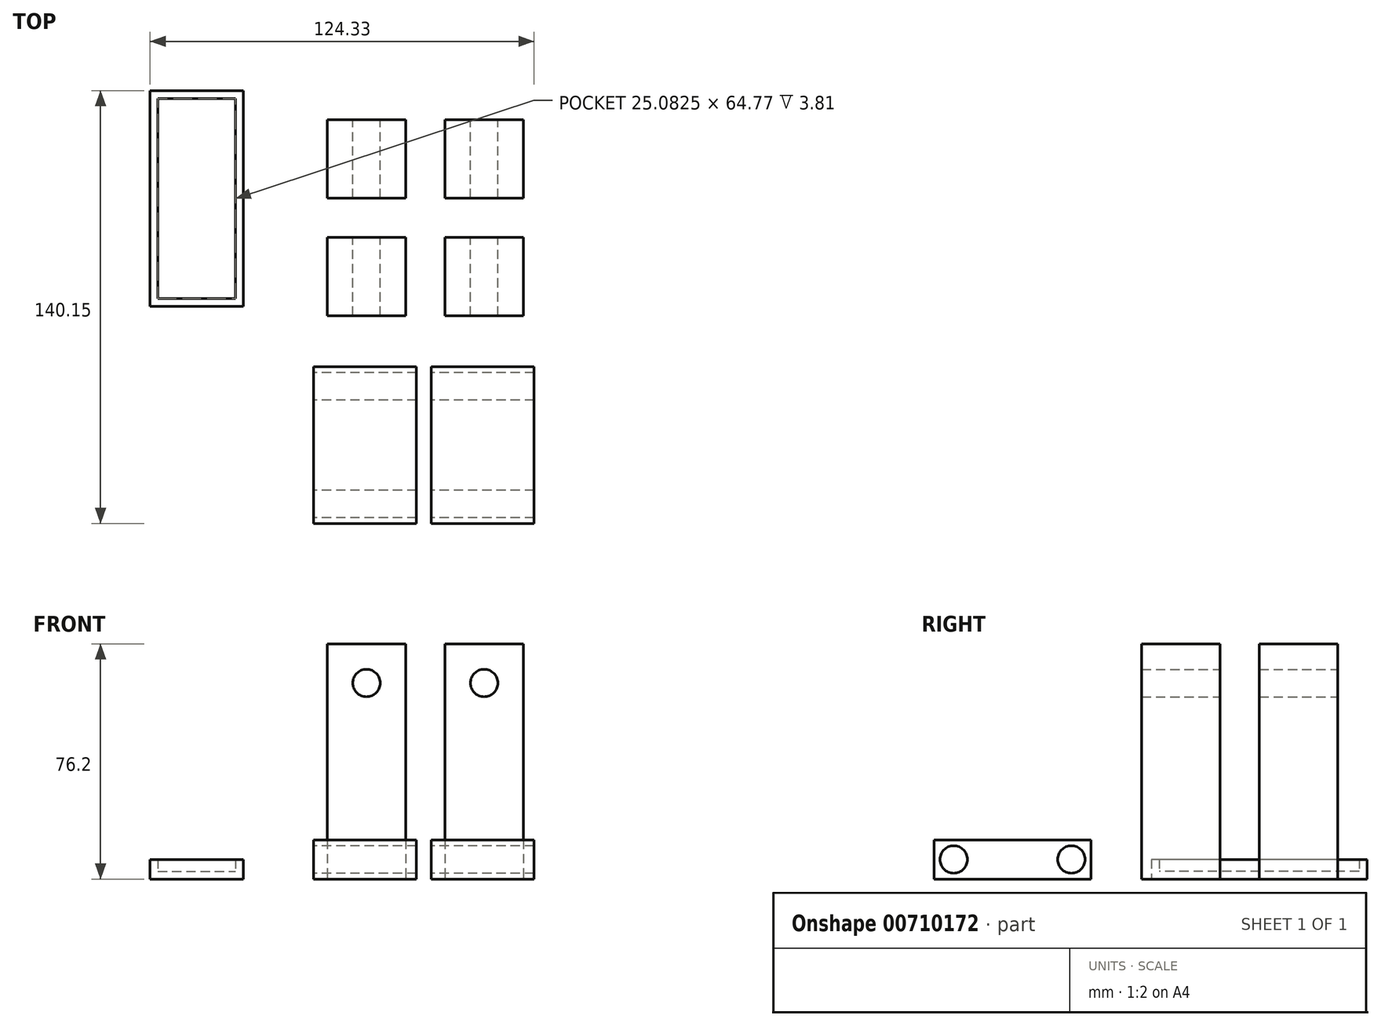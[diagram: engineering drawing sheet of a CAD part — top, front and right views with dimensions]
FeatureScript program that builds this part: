
annotation { "Feature Type Name" : "Feature", "Feature Type Description" : "" }
export const myFeature = defineFeature(function(context is Context, id is Id, definition is map)
    precondition{}
    {
        {
            var Q0;
            Q0=qCreatedBy(makeId("Top.planeOp"),FACE);
            var sketch = newSketch(context, id + "F0", { "sketchPlane" : qUnion([Q0])});
            skLineSegment(sketch, "E0.bottom", {"start": v(-52.9, 72.92) * mm, "end": v(-22.73, 72.92) * mm});
            skLineSegment(sketch, "E0.top", {"start": v(-52.9, 3.07) * mm, "end": v(-22.73, 3.07) * mm});
            skLineSegment(sketch, "E0.left", {"start": v(-52.9, 72.92) * mm, "end": v(-52.9, 3.07) * mm});
            skLineSegment(sketch, "E0.right", {"start": v(-22.73, 72.92) * mm, "end": v(-22.73, 3.07) * mm});
            skSolve(sketch);
        }
        {
            var Q0;
            Q0 = qSketchRegion(id + "F0", true);
            extrude(context, id + "F1", {"entities" : qUnion([Q0]), "depth" : 6.35 * mm, "offsetDistance" : 25.4 * mm});
        }
        {
            var Q0;
            Q0=makeQuery(id+"F1.opExtrude","CAP_FACE",FACE,{"disambiguationData":[OSD([sQuery(id+"F0.wireOp",EDGE,"E0.bottom"),sQuery(id+"F0.wireOp",EDGE,"E0.top"),sQuery(id+"F0.wireOp",EDGE,"E0.left"),sQuery(id+"F0.wireOp",EDGE,"E0.right")])],"isStart":false});
            shell(context, id + "F2", {"entities" : qUnion([Q0]), "thickness" : 2.54 * mm});
        }
        {
            var Q0;
            Q0=qCreatedBy(makeId("Front.planeOp"),FACE);
            var sketch = newSketch(context, id + "F3", { "sketchPlane" : qUnion([Q0])});
            skLineSegment(sketch, "E1.bottom", {"start": v(4.47, 76.2) * mm, "end": v(29.87, 76.2) * mm});
            skLineSegment(sketch, "E1.top", {"start": v(4.47, 0) * mm, "end": v(29.87, 0) * mm});
            skLineSegment(sketch, "E1.left", {"start": v(4.47, 76.2) * mm, "end": v(4.47, 0) * mm});
            skLineSegment(sketch, "E1.right", {"start": v(29.87, 76.2) * mm, "end": v(29.87, 0) * mm});
            skCircle(sketch, "E2", {"center": v(17.17, 63.5) * mm, "radius": 4.45 * mm});
            skPoint(sketch, "E3", {"position": v(17.17, 76.2) * mm});
            skSolve(sketch);
        }
        {
            var Q0;
            Q0 = qSketchRegion(id + "F3", true);
            extrude(context, id + "F4", {"entities" : qUnion([Q0]), "depth" : 25.4 * mm, "offsetDistance" : 25.4 * mm});
        }
        {
            var Q0;
            Q0=makeQuery(id+"F4.opExtrude","SWEPT_BODY",BODY,{"disambiguationData":[OSD([sQuery(id+"F3.wireOp",EDGE,"E1.bottom"),sQuery(id+"F3.wireOp",EDGE,"E1.top"),sQuery(id+"F3.wireOp",EDGE,"E1.left"),sQuery(id+"F3.wireOp",EDGE,"E1.right"),sQuery(id+"F3.wireOp",EDGE,"E2")])]});
            var Q1;
            Q1=makeQuery(id+"F4.opExtrude","SWEPT_EDGE",EDGE,{"disambiguationData":[OSD([sQuery(id+"F3.wireOp",EDGE,"E1.bottom"),sQuery(id+"F3.wireOp",EDGE,"E1.right")])]});
            transform(context, id + "F5", {"entities" : qUnion([Q0]), "transformType" : TransformType.TRANSLATION_ENTITY, "oppositeDirectionEntity" : false, "transformLine" : qUnion([Q1]), "makeCopy" : false});
        }
        {
            var Q0;
            Q0=makeQuery(id+"F4.opExtrude","SWEPT_BODY",BODY,{"disambiguationData":[OSD([sQuery(id+"F3.wireOp",EDGE,"E1.bottom"),sQuery(id+"F3.wireOp",EDGE,"E1.top"),sQuery(id+"F3.wireOp",EDGE,"E1.left"),sQuery(id+"F3.wireOp",EDGE,"E1.right"),sQuery(id+"F3.wireOp",EDGE,"E2")])]});
            transform(context, id + "F6", {"entities" : qUnion([Q0]), "transformType" : TransformType.TRANSLATION_3D, "dx" : 38.1 * mm, "dy" : 0 * mm, "dz" : 0 * mm, "makeCopy" : true});
        }
        {
            var Q0;
            Q0=makeQuery(id+"F4.opExtrude","SWEPT_BODY",BODY,{"disambiguationData":[OSD([sQuery(id+"F3.wireOp",EDGE,"E1.bottom"),sQuery(id+"F3.wireOp",EDGE,"E1.top"),sQuery(id+"F3.wireOp",EDGE,"E1.left"),sQuery(id+"F3.wireOp",EDGE,"E1.right"),sQuery(id+"F3.wireOp",EDGE,"E2")])]});
            transform(context, id + "F7", {"entities" : qUnion([Q0]), "transformType" : TransformType.TRANSLATION_3D, "dx" : 0 * mm, "dy" : 38.1 * mm, "dz" : 0 * mm, "makeCopy" : true});
        }
        {
            var Q0;
            Q0=makeQuery(id+"F4.opExtrude","SWEPT_BODY",BODY,{"disambiguationData":[OSD([sQuery(id+"F3.wireOp",EDGE,"E1.bottom"),sQuery(id+"F3.wireOp",EDGE,"E1.top"),sQuery(id+"F3.wireOp",EDGE,"E1.left"),sQuery(id+"F3.wireOp",EDGE,"E1.right"),sQuery(id+"F3.wireOp",EDGE,"E2")])]});
            transform(context, id + "F8", {"entities" : qUnion([Q0]), "transformType" : TransformType.TRANSLATION_3D, "dx" : 38.1 * mm, "dy" : 38.1 * mm, "dz" : 0 * mm, "makeCopy" : true});
        }
        {
            var Q0;
            Q0=qCreatedBy(makeId("Right.planeOp"),FACE);
            var sketch = newSketch(context, id + "F9", { "sketchPlane" : qUnion([Q0])});
            skLineSegment(sketch, "E4.bottom", {"start": v(-67.23, 12.7) * mm, "end": v(-16.43, 12.7) * mm});
            skLineSegment(sketch, "E4.top", {"start": v(-67.23, 0) * mm, "end": v(-16.43, 0) * mm});
            skLineSegment(sketch, "E4.left", {"start": v(-67.23, 12.7) * mm, "end": v(-67.23, 0) * mm});
            skLineSegment(sketch, "E4.right", {"start": v(-16.43, 12.7) * mm, "end": v(-16.43, 0) * mm});
            skCircle(sketch, "E5", {"center": v(-60.88, 6.35) * mm, "radius": 4.45 * mm});
            skPoint(sketch, "E6", {"position": v(-67.23, 6.35) * mm});
            skCircle(sketch, "E7", {"center": v(-22.78, 6.35) * mm, "radius": 4.45 * mm});
            skPoint(sketch, "E8", {"position": v(-16.43, 6.35) * mm});
            skSolve(sketch);
        }
        {
            var Q0;
            Q0 = qSketchRegion(id + "F9", true);
            extrude(context, id + "F10", {"entities" : qUnion([Q0]), "depth" : 33.34 * mm, "offsetDistance" : 25.4 * mm});
        }
        {
            var Q0;
            Q0=makeQuery(id+"F10.opExtrude","SWEPT_BODY",BODY,{"disambiguationData":[OSD([sQuery(id+"F9.wireOp",EDGE,"E4.bottom"),sQuery(id+"F9.wireOp",EDGE,"E4.top"),sQuery(id+"F9.wireOp",EDGE,"E4.left"),sQuery(id+"F9.wireOp",EDGE,"E4.right"),sQuery(id+"F9.wireOp",EDGE,"E5"),sQuery(id+"F9.wireOp",EDGE,"E7")])]});
            transform(context, id + "F11", {"entities" : qUnion([Q0]), "transformType" : TransformType.TRANSLATION_3D, "dx" : 38.1 * mm, "dy" : 0 * mm, "dz" : 0 * mm, "makeCopy" : true});
        }
    });
